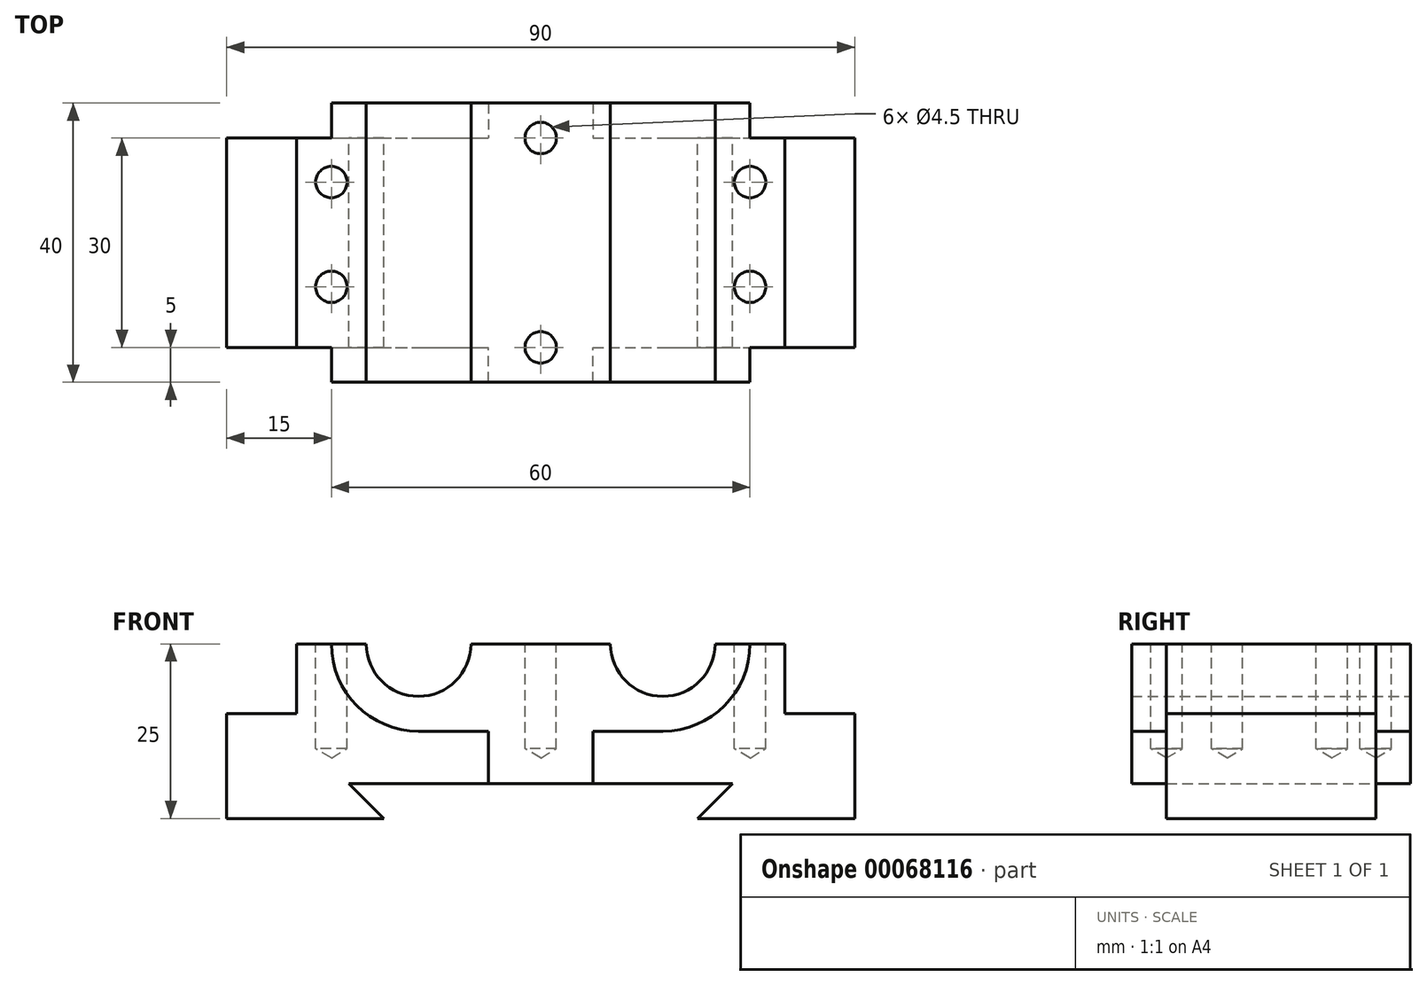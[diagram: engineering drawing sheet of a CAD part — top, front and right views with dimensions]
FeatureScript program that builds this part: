
annotation { "Feature Type Name" : "Feature", "Feature Type Description" : "" }
export const myFeature = defineFeature(function(context is Context, id is Id, definition is map)
    precondition{}
    {
        {
            var Q0;
            Q0=qCreatedBy(makeId("Front.planeOp"),FACE);
            var sketch = newSketch(context, id + "F0", { "sketchPlane" : qUnion([Q0])});
            skLineSegment(sketch, "E0", {"start": v(-45, -5) * mm, "end": v(-22.5, -5) * mm});
            skLineSegment(sketch, "E1", {"start": v(-22.5, -5) * mm, "end": v(-27.5, 0) * mm});
            skLineSegment(sketch, "E2", {"start": v(-27.5, 0) * mm, "end": v(27.5, 0) * mm});
            skLineSegment(sketch, "E3", {"start": v(27.5, 0) * mm, "end": v(22.5, -5) * mm});
            skLineSegment(sketch, "E4", {"start": v(22.5, -5) * mm, "end": v(45, -5) * mm});
            skLineSegment(sketch, "E5", {"start": v(45, -5) * mm, "end": v(45, 10) * mm});
            skLineSegment(sketch, "E6", {"start": v(45, 10) * mm, "end": v(35, 10) * mm});
            skLineSegment(sketch, "E7", {"start": v(35, 10) * mm, "end": v(35, 20) * mm});
            skLineSegment(sketch, "E8", {"start": v(35, 20) * mm, "end": v(25, 20) * mm});
            skLineSegment(sketch, "E9", {"start": v(-35, 20) * mm, "end": v(-35, 10) * mm});
            skLineSegment(sketch, "E10", {"start": v(-35, 10) * mm, "end": v(-45, 10) * mm});
            skLineSegment(sketch, "E11", {"start": v(-45, 10) * mm, "end": v(-45, -5) * mm});
            skArc(sketch, "E12", {"start": v(-25, 20) * mm, "mid": v(-17.5, 12.5) * mm, "end": v(-10, 20) * mm});
            skArc(sketch, "E13", {"start": v(10, 20) * mm, "mid": v(17.5, 12.5) * mm, "end": v(25, 20) * mm});
            skLineSegment(sketch, "E14.trimOffspring", {"start": v(10, 20) * mm, "end": v(-10, 20) * mm});
            skLineSegment(sketch, "E15.trimOffspring", {"start": v(-25, 20) * mm, "end": v(-35, 20) * mm});
            skSolve(sketch);
        }
        {
            var Q0;
            Q0=makeQuery(id+"F0.imprint","IMPRINT",FACE,{"disambiguationData":[TD([[makeQuery(id+"F0.imprint","IMPRINT",EDGE,{"derivedFrom":sQuery(id+"F0.wireOp",EDGE,"E0")}),1.0]])]});
            extrude(context, id + "F1", {"entities" : qUnion([Q0]), "endBound" : BoundingType.SYMMETRIC, "depth" : 30 * mm});
        }
        {
            var Q0;
            Q0=makeQuery(id+"F1.opExtrude","CAP_FACE",FACE,{"disambiguationData":[OSD([sQuery(id+"F0.wireOp",EDGE,"E0"),sQuery(id+"F0.wireOp",EDGE,"E1"),sQuery(id+"F0.wireOp",EDGE,"E2"),sQuery(id+"F0.wireOp",EDGE,"E3"),sQuery(id+"F0.wireOp",EDGE,"E4"),sQuery(id+"F0.wireOp",EDGE,"E5"),sQuery(id+"F0.wireOp",EDGE,"E6"),sQuery(id+"F0.wireOp",EDGE,"E7"),sQuery(id+"F0.wireOp",EDGE,"E8"),sQuery(id+"F0.wireOp",EDGE,"E9"),sQuery(id+"F0.wireOp",EDGE,"E10"),sQuery(id+"F0.wireOp",EDGE,"E11"),sQuery(id+"F0.wireOp",EDGE,"E12"),sQuery(id+"F0.wireOp",EDGE,"E13"),sQuery(id+"F0.wireOp",EDGE,"E14.trimOffspring"),sQuery(id+"F0.wireOp",EDGE,"E15.trimOffspring")])],"isStart":false});
            var sketch = newSketch(context, id + "F2", { "sketchPlane" : qUnion([Q0])});
            skArc(sketch, "E16", {"start": v(-30, 20) * mm, "mid": v(-26.34, 11.16) * mm, "end": v(-17.5, 7.5) * mm});
            skArc(sketch, "E17", {"start": v(17.5, 7.5) * mm, "mid": v(26.34, 11.16) * mm, "end": v(30, 20) * mm});
            skLineSegment(sketch, "E18", {"start": v(-17.5, 7.5) * mm, "end": v(-7.5, 7.5) * mm});
            skLineSegment(sketch, "E19", {"start": v(-7.5, 7.5) * mm, "end": v(-7.5, 0) * mm});
            skLineSegment(sketch, "E20", {"start": v(-7.5, 0) * mm, "end": v(7.5, 0) * mm});
            skLineSegment(sketch, "E21", {"start": v(7.5, 0) * mm, "end": v(7.5, 7.5) * mm});
            skLineSegment(sketch, "E22", {"start": v(7.5, 7.5) * mm, "end": v(17.5, 7.5) * mm});
            skLineSegment(sketch, "E23.0", {"start": v(-25, 20) * mm, "end": v(-30, 20) * mm});
            skArc(sketch, "E24.0", {"start": v(-25, 20) * mm, "mid": v(-17.5, 12.5) * mm, "end": v(-10, 20) * mm});
            skLineSegment(sketch, "E25.0", {"start": v(10, 20) * mm, "end": v(-10, 20) * mm});
            skArc(sketch, "E26.0", {"start": v(10, 20) * mm, "mid": v(17.5, 12.5) * mm, "end": v(25, 20) * mm});
            skLineSegment(sketch, "E27.0", {"start": v(35, 20) * mm, "end": v(25, 20) * mm});
            skPoint(sketch, "E28.orphan", {"position": v(-35, 20) * mm});
            skSolve(sketch);
        }
        {
            var Q0;
            Q0=makeQuery(id+"F2.imprint","IMPRINT",FACE,{"disambiguationData":[TD([[makeQuery(id+"F2.imprint","IMPRINT",EDGE,{"derivedFrom":sQuery(id+"F2.wireOp",EDGE,"E16")}),1.0]])]});
            extrude(context, id + "F3", {"entities" : qUnion([Q0]), "operationType" : NewBodyOperationType.ADD, "depth" : 5 * mm});
        }
        {
            var Q0;
            Q0=makeQuery(id+"F1.opExtrude","SWEPT_BODY",BODY,{"disambiguationData":[OSD([sQuery(id+"F0.wireOp",EDGE,"E0"),sQuery(id+"F0.wireOp",EDGE,"E1"),sQuery(id+"F0.wireOp",EDGE,"E2"),sQuery(id+"F0.wireOp",EDGE,"E3"),sQuery(id+"F0.wireOp",EDGE,"E4"),sQuery(id+"F0.wireOp",EDGE,"E5"),sQuery(id+"F0.wireOp",EDGE,"E6"),sQuery(id+"F0.wireOp",EDGE,"E7"),sQuery(id+"F0.wireOp",EDGE,"E8"),sQuery(id+"F0.wireOp",EDGE,"E9"),sQuery(id+"F0.wireOp",EDGE,"E10"),sQuery(id+"F0.wireOp",EDGE,"E11"),sQuery(id+"F0.wireOp",EDGE,"E12"),sQuery(id+"F0.wireOp",EDGE,"E13"),sQuery(id+"F0.wireOp",EDGE,"E14.trimOffspring"),sQuery(id+"F0.wireOp",EDGE,"E15.trimOffspring")])]});
            var Q1;
            Q1=qCreatedBy(makeId("Front.planeOp"),FACE);
            mirror(context, id + "F4", {"operationType" : NewBodyOperationType.ADD, "entities" : qUnion([Q0]), "mirrorPlane" : qUnion([Q1])});
        }
        {
            var Q0;
            {var subQ0=makeQuery(id+"F3.boolean.opBoolean","MERGE",FACE,{"derivedFrom":[makeQuery(id+"F1.opExtrude","SWEPT_FACE",FACE,{"disambiguationData":[OSD([sQuery(id+"F0.wireOp",EDGE,"E14.trimOffspring")])]}),makeQuery(id+"F3.opExtrude","SWEPT_FACE",FACE,{"disambiguationData":[OSD([sQuery(id+"F2.wireOp",EDGE,"E25.0")])]})]});Q0=makeQuery(id+"F4.boolean.opBoolean","MERGE",FACE,{"derivedFrom":[subQ0,makeQuery(id+"F4.opPattern","COPY",FACE,{"derivedFrom":subQ0,"instanceName":"1"})]});}
            var sketch = newSketch(context, id + "F5", { "sketchPlane" : qUnion([Q0])});
            skPoint(sketch, "E29", {"position": v(-30, 8.69) * mm});
            skPoint(sketch, "E30", {"position": v(-30, -6.31) * mm});
            skPoint(sketch, "E31", {"position": v(0, -15) * mm});
            skPoint(sketch, "E32", {"position": v(0, 15) * mm});
            skPoint(sketch, "E33", {"position": v(30, 8.69) * mm});
            skPoint(sketch, "E34", {"position": v(30, -6.31) * mm});
            skSolve(sketch);
        }
        {
            var Q0;
            Q0=sQuery(id+"F5.wireOp",VERTEX,"E29");
            var Q1;
            Q1=sQuery(id+"F5.wireOp",VERTEX,"E30");
            var Q2;
            Q2=sQuery(id+"F5.wireOp",VERTEX,"E32");
            var Q3;
            Q3=sQuery(id+"F5.wireOp",VERTEX,"E31");
            var Q4;
            Q4=sQuery(id+"F5.wireOp",VERTEX,"E33");
            var Q5;
            Q5=sQuery(id+"F5.wireOp",VERTEX,"E34");
            var Q6;
            Q6=makeQuery(id+"F1.opExtrude","SWEPT_BODY",BODY,{"disambiguationData":[OSD([sQuery(id+"F0.wireOp",EDGE,"E0"),sQuery(id+"F0.wireOp",EDGE,"E1"),sQuery(id+"F0.wireOp",EDGE,"E2"),sQuery(id+"F0.wireOp",EDGE,"E3"),sQuery(id+"F0.wireOp",EDGE,"E4"),sQuery(id+"F0.wireOp",EDGE,"E5"),sQuery(id+"F0.wireOp",EDGE,"E6"),sQuery(id+"F0.wireOp",EDGE,"E7"),sQuery(id+"F0.wireOp",EDGE,"E8"),sQuery(id+"F0.wireOp",EDGE,"E9"),sQuery(id+"F0.wireOp",EDGE,"E10"),sQuery(id+"F0.wireOp",EDGE,"E11"),sQuery(id+"F0.wireOp",EDGE,"E12"),sQuery(id+"F0.wireOp",EDGE,"E13"),sQuery(id+"F0.wireOp",EDGE,"E14.trimOffspring"),sQuery(id+"F0.wireOp",EDGE,"E15.trimOffspring")])]});
            hole(context, id + "F6", {"style" : HoleStyle.SIMPLE, "holeDiameter" : 4.5 * mm, "endStyle" : HoleEndStyle.BLIND, "holeDepth" : 15 * mm, "locations" : qUnion([Q0, Q1, Q2, Q3, Q4, Q5]), "scope" : qUnion([Q6])});
        }
    });
